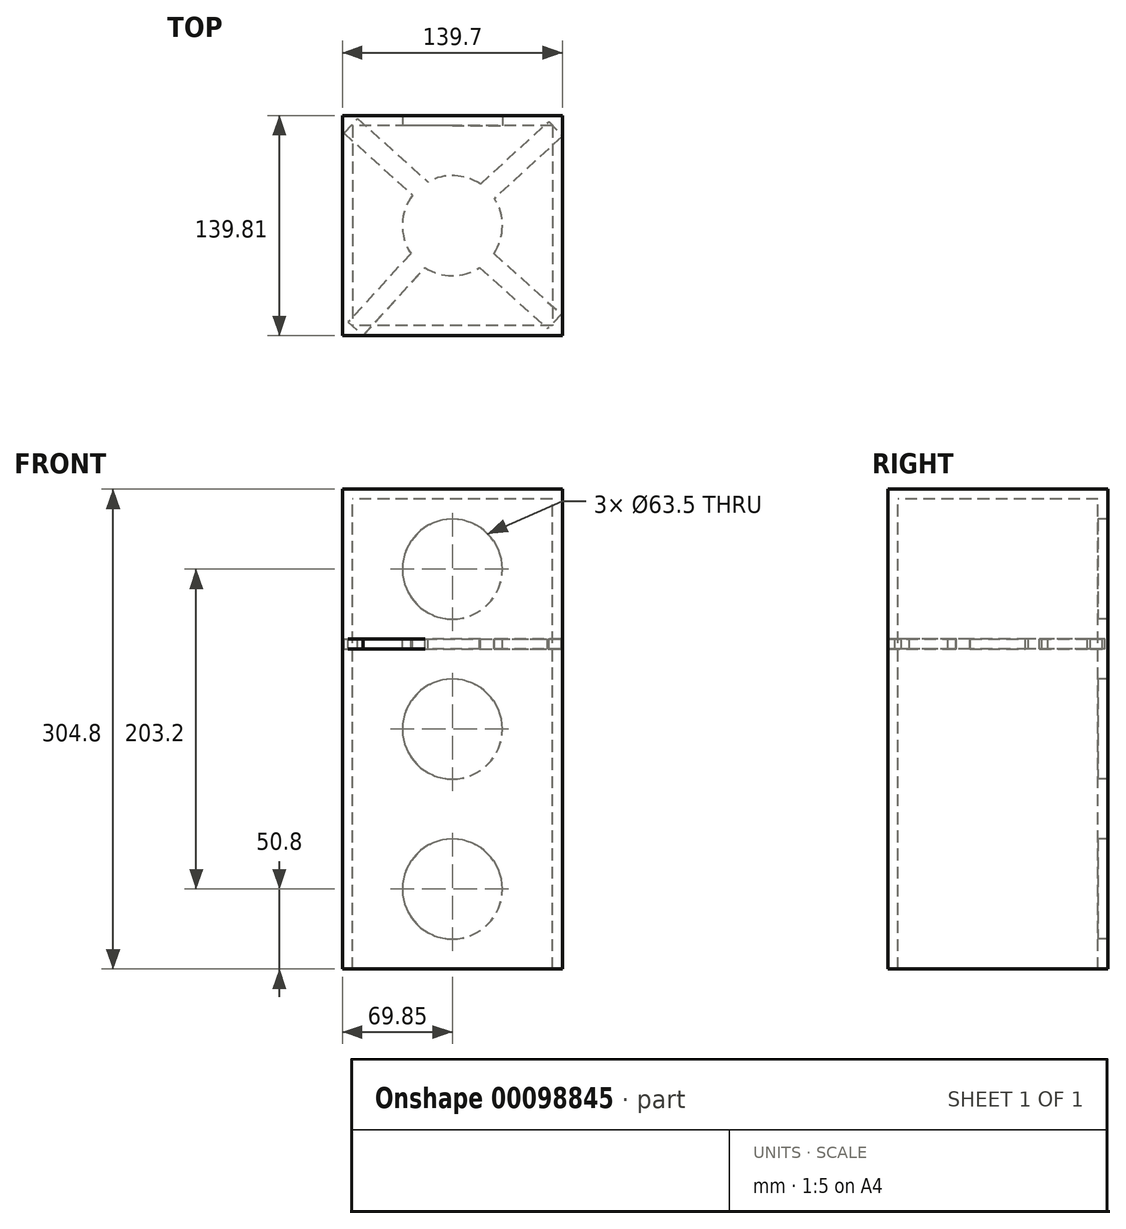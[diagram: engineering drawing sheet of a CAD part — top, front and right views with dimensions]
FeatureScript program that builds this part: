
annotation { "Feature Type Name" : "Feature", "Feature Type Description" : "" }
export const myFeature = defineFeature(function(context is Context, id is Id, definition is map)
    precondition{}
    {
        {
            var Q0;
            Q0=qCreatedBy(makeId("Front.planeOp"),FACE);
            var sketch = newSketch(context, id + "F0", { "sketchPlane" : qUnion([Q0])});
            skLineSegment(sketch, "E0.bottom", {"start": v(69.85, -152.4) * mm, "end": v(-69.85, -152.4) * mm});
            skLineSegment(sketch, "E0.top", {"start": v(69.85, 152.4) * mm, "end": v(-69.85, 152.4) * mm});
            skLineSegment(sketch, "E0.left", {"start": v(69.85, -152.4) * mm, "end": v(69.85, 152.4) * mm});
            skLineSegment(sketch, "E0.right", {"start": v(-69.85, -152.4) * mm, "end": v(-69.85, 152.4) * mm});
            skPoint(sketch, "E0.middle", {"position": v(0, 0) * mm});
            skSolve(sketch);
        }
        {
            var Q0;
            Q0 = qSketchRegion(id + "F0", true);
            extrude(context, id + "F1", {"entities" : qUnion([Q0]), "endBound" : BoundingType.SYMMETRIC, "depth" : 139.7 * mm});
        }
        {
            var Q0;
            Q0=qCreatedBy(makeId("Top.planeOp"),FACE);
            var sketch = newSketch(context, id + "F2", { "sketchPlane" : qUnion([Q0])});
            skLineSegment(sketch, "E1.bottom", {"start": v(63.5, 63.5) * mm, "end": v(-63.5, 63.5) * mm});
            skLineSegment(sketch, "E1.top", {"start": v(63.5, -63.5) * mm, "end": v(-63.5, -63.5) * mm});
            skLineSegment(sketch, "E1.left", {"start": v(63.5, 63.5) * mm, "end": v(63.5, -63.5) * mm});
            skLineSegment(sketch, "E1.right", {"start": v(-63.5, 63.5) * mm, "end": v(-63.5, -63.5) * mm});
            skPoint(sketch, "E1.middle", {"position": v(0, 0) * mm});
            skSolve(sketch);
        }
        {
            var Q0;
            Q0 = qSketchRegion(id + "F2", true);
            extrude(context, id + "F3", {"entities" : qUnion([Q0]), "operationType" : NewBodyOperationType.REMOVE, "oppositeDirection" : true, "depth" : 152.4 * mm, "hasSecondDirection" : true, "secondDirectionOppositeDirection" : false, "secondDirectionDepth" : 146.05 * mm});
        }
        {
            var Q0;
            Q0=qCreatedBy(makeId("Front.planeOp"),FACE);
            var sketch = newSketch(context, id + "F4", { "sketchPlane" : qUnion([Q0])});
            skCircle(sketch, "E2", {"center": v(0, 0) * mm, "radius": 31.75 * mm});
            skLineSegment(sketch, "E3", {"start": v(0, 0) * mm, "end": v(0, 101.6) * mm, "construction": true});
            skCircle(sketch, "E4", {"center": v(0, 101.6) * mm, "radius": 31.75 * mm});
            skLineSegment(sketch, "E5", {"start": v(0, 0) * mm, "end": v(0, -101.6) * mm, "construction": true});
            skCircle(sketch, "E6", {"center": v(0, -101.6) * mm, "radius": 31.75 * mm});
            skSolve(sketch);
        }
        {
            var Q0;
            Q0 = qSketchRegion(id + "F4", true);
            extrude(context, id + "F5", {"entities" : qUnion([Q0]), "operationType" : NewBodyOperationType.REMOVE, "oppositeDirection" : true, "depth" : 127 * mm});
        }
        {
            var Q0;
            Q0=qCreatedBy(makeId("Top.planeOp"),FACE);
            cPlane(context, id + "F6", {"entities" : qUnion([Q0]), "cplaneType" : CPlaneType.OFFSET, "offset" : 57.15 * mm, "width" : 152.4 * mm, "height" : 152.4 * mm});
        }
        {
            var Q0;
            Q0=qCreatedBy(id+"F6.planeOp",FACE);
            var sketch = newSketch(context, id + "F7", { "sketchPlane" : qUnion([Q0])});
            skCircle(sketch, "E7", {"center": v(0, 0) * mm, "radius": 31.75 * mm});
            skLineSegment(sketch, "E8", {"start": v(-60.23, 67.91) * mm, "end": v(-12.99, 25.49) * mm});
            skLineSegment(sketch, "E9", {"start": v(-68.93, 58.65) * mm, "end": v(-21.68, 16.23) * mm});
            skLineSegment(sketch, "E10", {"start": v(-21.68, 16.23) * mm, "end": v(-12.99, 25.49) * mm});
            skLineSegment(sketch, "E11", {"start": v(-68.93, 58.65) * mm, "end": v(-60.23, 67.91) * mm});
            skLineSegment(sketch, "E12", {"start": v(15.2, -24.84) * mm, "end": v(60.57, -65.56) * mm});
            skLineSegment(sketch, "E13", {"start": v(23.84, -15.52) * mm, "end": v(69.2, -56.25) * mm});
            skLineSegment(sketch, "E14", {"start": v(69.2, -56.25) * mm, "end": v(60.57, -65.56) * mm});
            skLineSegment(sketch, "E15", {"start": v(23.84, -15.52) * mm, "end": v(15.2, -24.84) * mm});
            skLineSegment(sketch, "E16", {"start": v(-23.4, -14.47) * mm, "end": v(-66.18, -61.4) * mm});
            skLineSegment(sketch, "E17", {"start": v(-66.18, -61.4) * mm, "end": v(-56.79, -69.96) * mm});
            skLineSegment(sketch, "E18", {"start": v(-56.79, -69.96) * mm, "end": v(-14.02, -23.02) * mm});
            skLineSegment(sketch, "E19", {"start": v(-14.02, -23.02) * mm, "end": v(-23.4, -14.47) * mm});
            skLineSegment(sketch, "E20", {"start": v(15.32, 24.12) * mm, "end": v(61.26, 66.1) * mm});
            skLineSegment(sketch, "E21", {"start": v(61.26, 66.1) * mm, "end": v(69.83, 56.72) * mm});
            skLineSegment(sketch, "E22", {"start": v(69.83, 56.72) * mm, "end": v(23.88, 14.74) * mm});
            skLineSegment(sketch, "E23", {"start": v(23.88, 14.74) * mm, "end": v(15.32, 24.12) * mm});
            skSolve(sketch);
        }
        {
            var Q0;
            Q0 = qSketchRegion(id + "F7", true);
            extrude(context, id + "F8", {"entities" : qUnion([Q0]), "oppositeDirection" : true, "depth" : 6.35 * mm});
        }
        {
            var Q0;
            Q0=qCreatedBy(makeId("Top.planeOp"),FACE);
            cPlane(context, id + "F9", {"entities" : qUnion([Q0]), "cplaneType" : CPlaneType.OFFSET, "offset" : 44.45 * mm, "width" : 152.4 * mm, "height" : 152.4 * mm});
        }
        {
            var Q0;
            Q0=qCreatedBy(id+"F9.planeOp",FACE);
            var sketch = newSketch(context, id + "F10", { "sketchPlane" : qUnion([Q0])});
            skLineSegment(sketch, "E24", {"start": v(0, 0) * mm, "end": v(0, -6.35) * mm});
            skLineSegment(sketch, "E25", {"start": v(0, 0) * mm, "end": v(0, 6.35) * mm});
            skArc(sketch, "E26", {"start": v(0, 6.35) * mm, "mid": v(-6.35, 0) * mm, "end": v(0, -6.35) * mm});
            skSolve(sketch);
        }
        {
            var Q0;
            Q0=makeQuery(id+"F10.imprint","IMPRINT",FACE,{"disambiguationData":[TD([[makeQuery(id+"F10.imprint","IMPRINT",EDGE,{"derivedFrom":sQuery(id+"F10.wireOp",EDGE,"E24")}),-1.0]])]});
            var Q1;
            Q1=sQuery(id+"F10.wireOp",EDGE,"E24");
            revolve(context, id + "F11", {"operationType" : NewBodyOperationType.REMOVE, "entities" : qUnion([Q0]), "axis" : qUnion([Q1]), "revolveType" : RevolveType.FULL, "oppositeDirection" : true});
        }
    });
